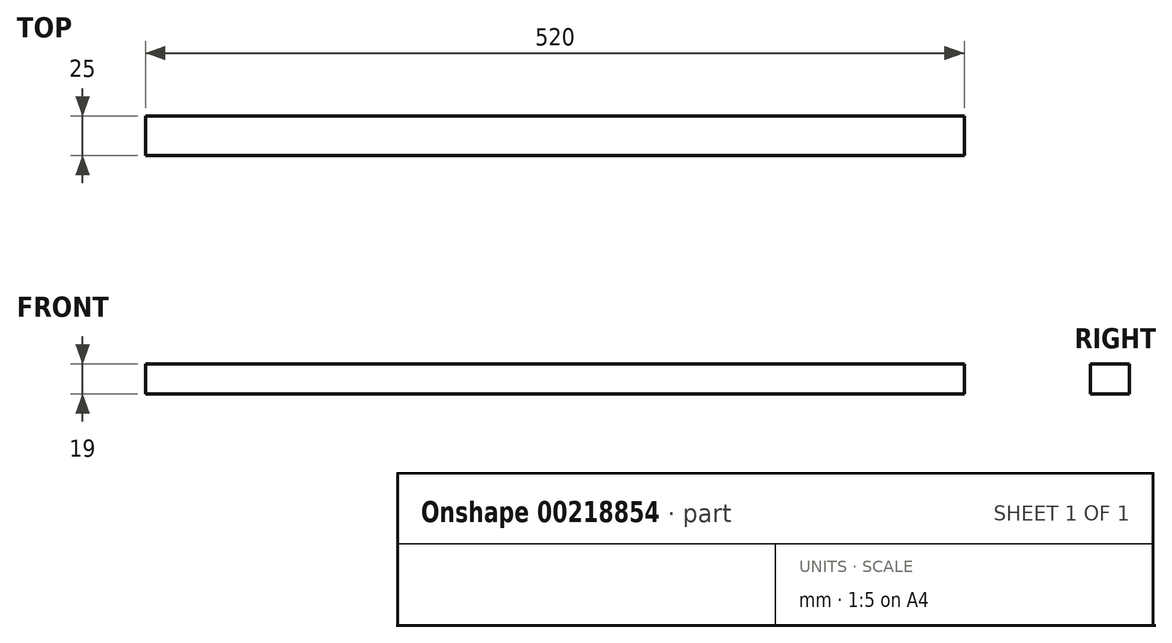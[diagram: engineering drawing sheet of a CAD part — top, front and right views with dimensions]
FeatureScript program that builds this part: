
annotation { "Feature Type Name" : "Feature", "Feature Type Description" : "" }
export const myFeature = defineFeature(function(context is Context, id is Id, definition is map)
    precondition{}
    {
        {
            var Q0;
            Q0=qCreatedBy(makeId("Front.planeOp"),FACE);
            var sketch = newSketch(context, id + "F0", { "sketchPlane" : qUnion([Q0])});
            skLineSegment(sketch, "E0.bottom", {"start": v(-274.43, -33.52) * mm, "end": v(245.57, -33.52) * mm});
            skLineSegment(sketch, "E0.top", {"start": v(-274.43, -52.52) * mm, "end": v(245.57, -52.52) * mm});
            skLineSegment(sketch, "E0.left", {"start": v(-274.43, -33.52) * mm, "end": v(-274.43, -52.52) * mm});
            skLineSegment(sketch, "E0.right", {"start": v(245.57, -33.52) * mm, "end": v(245.57, -52.52) * mm});
            skSolve(sketch);
        }
        {
            var Q0;
            Q0=qSketchRegion(id+"F0",true);
            extrude(context, id + "F1", {"entities" : qUnion([Q0]), "depth" : 25 * mm});
        }
    });
